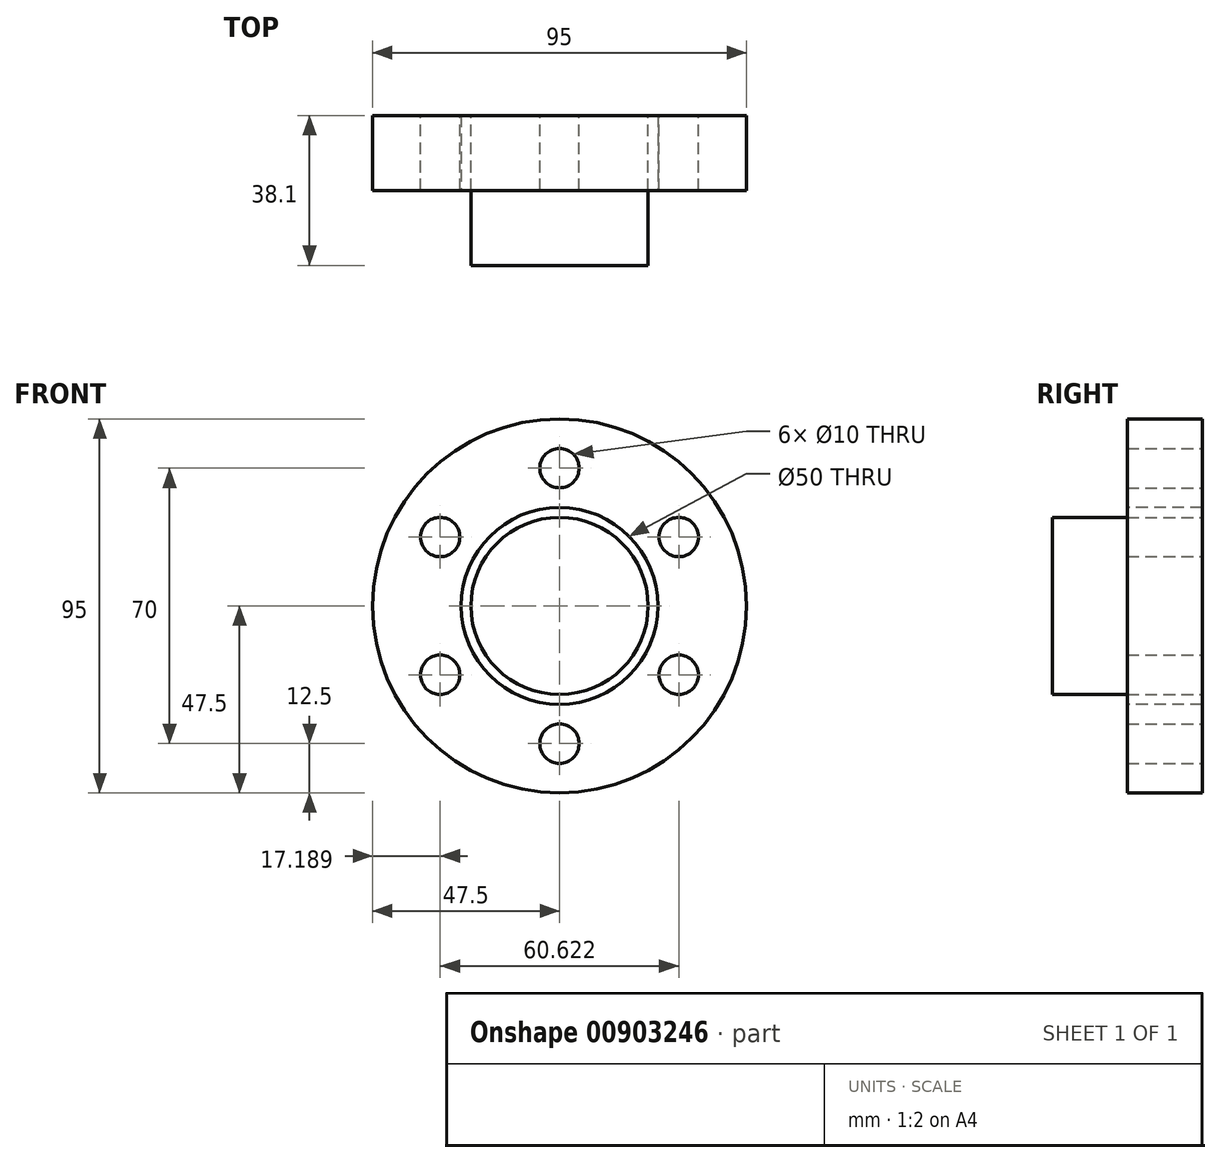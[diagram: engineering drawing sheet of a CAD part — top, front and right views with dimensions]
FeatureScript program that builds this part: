
annotation { "Feature Type Name" : "Feature", "Feature Type Description" : "" }
export const myFeature = defineFeature(function(context is Context, id is Id, definition is map)
    precondition{}
    {
        {
            var Q0;
            Q0=qCreatedBy(makeId("Front.planeOp"),FACE);
            var sketch = newSketch(context, id + "F0", { "sketchPlane" : qUnion([Q0])});
            skCircle(sketch, "E0", {"center": v(0, 0) * mm, "radius": 47.5 * mm});
            skCircle(sketch, "E1", {"center": v(0, 0) * mm, "radius": 35 * mm, "construction": true});
            skLineSegment(sketch, "E2", {"start": v(0, 0) * mm, "end": v(0, 87.92) * mm});
            skCircle(sketch, "E3", {"center": v(0, 35) * mm, "radius": 5 * mm});
            skCircle(sketch, "E4.1.0", {"center": v(-30.31, 17.5) * mm, "radius": 5 * mm});
            skCircle(sketch, "E4.2.0", {"center": v(-30.31, -17.5) * mm, "radius": 5 * mm});
            skCircle(sketch, "E4.3.0", {"center": v(0, -35) * mm, "radius": 5 * mm});
            skCircle(sketch, "E4.4.0", {"center": v(30.31, -17.5) * mm, "radius": 5 * mm});
            skCircle(sketch, "E4.5.0", {"center": v(30.31, 17.5) * mm, "radius": 5 * mm});
            skSolve(sketch);
        }
        {
            var Q0;
            Q0=makeQuery(id+"F0.imprint","IMPRINT",FACE,{"disambiguationData":[TD([[makeQuery(id+"F0.imprint","IMPRINT",EDGE,{"derivedFrom":sQuery(id+"F0.wireOp",EDGE,"E0")}),1.0]])]});
            extrude(context, id + "F1", {"entities" : qUnion([Q0]), "depth" : 19.05 * mm});
        }
        {
            var Q0;
            Q0=makeQuery(id+"F1.opExtrude","CAP_FACE",FACE,{"disambiguationData":[OSD([sQuery(id+"F0.wireOp",EDGE,"E0"),sQuery(id+"F0.wireOp",EDGE,"47804e7a-2431-4f3c-b785-4ff43a304412"),sQuery(id+"F0.wireOp",EDGE,"d4718459-af55-4dad-8911-bd223aa27aa5.1.0"),sQuery(id+"F0.wireOp",EDGE,"d4718459-af55-4dad-8911-bd223aa27aa5.2.0"),sQuery(id+"F0.wireOp",EDGE,"d4718459-af55-4dad-8911-bd223aa27aa5.3.0"),sQuery(id+"F0.wireOp",EDGE,"d4718459-af55-4dad-8911-bd223aa27aa5.4.0"),sQuery(id+"F0.wireOp",EDGE,"d4718459-af55-4dad-8911-bd223aa27aa5.5.0")])],"isStart":false});
            var sketch = newSketch(context, id + "F2", { "sketchPlane" : qUnion([Q0])});
            skCircle(sketch, "E5", {"center": v(0, 0) * mm, "radius": 22.5 * mm});
            skSolve(sketch);
        }
        {
            var Q0;
            Q0=makeQuery(id+"F2.imprint","IMPRINT",FACE,{"disambiguationData":[TD([[makeQuery(id+"F2.imprint","IMPRINT",EDGE,{"derivedFrom":sQuery(id+"F2.wireOp",EDGE,"E5")}),1.0]])]});
            extrude(context, id + "F3", {"entities" : qUnion([Q0]), "operationType" : NewBodyOperationType.ADD, "depth" : 19.05 * mm});
        }
        {
            var Q0;
            Q0=makeQuery(id+"F3.boolean.opBoolean","SPLIT",FACE,{"disambiguationData":[TD([makeQuery(id+"F3.opExtrude","SWEPT_FACE",FACE,{"disambiguationData":[OSD([sQuery(id+"F2.wireOp",EDGE,"E5")])]})])],"derivedFrom":makeQuery(id+"F1.opExtrude","CAP_FACE",FACE,{"disambiguationData":[OSD([sQuery(id+"F0.wireOp",EDGE,"E0"),sQuery(id+"F0.wireOp",EDGE,"47804e7a-2431-4f3c-b785-4ff43a304412"),sQuery(id+"F0.wireOp",EDGE,"d4718459-af55-4dad-8911-bd223aa27aa5.1.0"),sQuery(id+"F0.wireOp",EDGE,"d4718459-af55-4dad-8911-bd223aa27aa5.2.0"),sQuery(id+"F0.wireOp",EDGE,"d4718459-af55-4dad-8911-bd223aa27aa5.3.0"),sQuery(id+"F0.wireOp",EDGE,"d4718459-af55-4dad-8911-bd223aa27aa5.4.0"),sQuery(id+"F0.wireOp",EDGE,"d4718459-af55-4dad-8911-bd223aa27aa5.5.0")])],"isStart":false})});
            var sketch = newSketch(context, id + "F4", { "sketchPlane" : qUnion([Q0])});
            skCircle(sketch, "E6", {"center": v(0, 0) * mm, "radius": 25 * mm});
            skSolve(sketch);
        }
        {
            var Q0;
            Q0=makeQuery(id+"F4.imprint","IMPRINT",FACE,{"disambiguationData":[TD([[makeQuery(id+"F4.imprint","IMPRINT",EDGE,{"derivedFrom":sQuery(id+"F4.wireOp",EDGE,"E6")}),1.0]])]});
            extrude(context, id + "F5", {"entities" : qUnion([Q0]), "operationType" : NewBodyOperationType.REMOVE, "oppositeDirection" : true, "depth" : 25.4 * mm});
        }
    });
